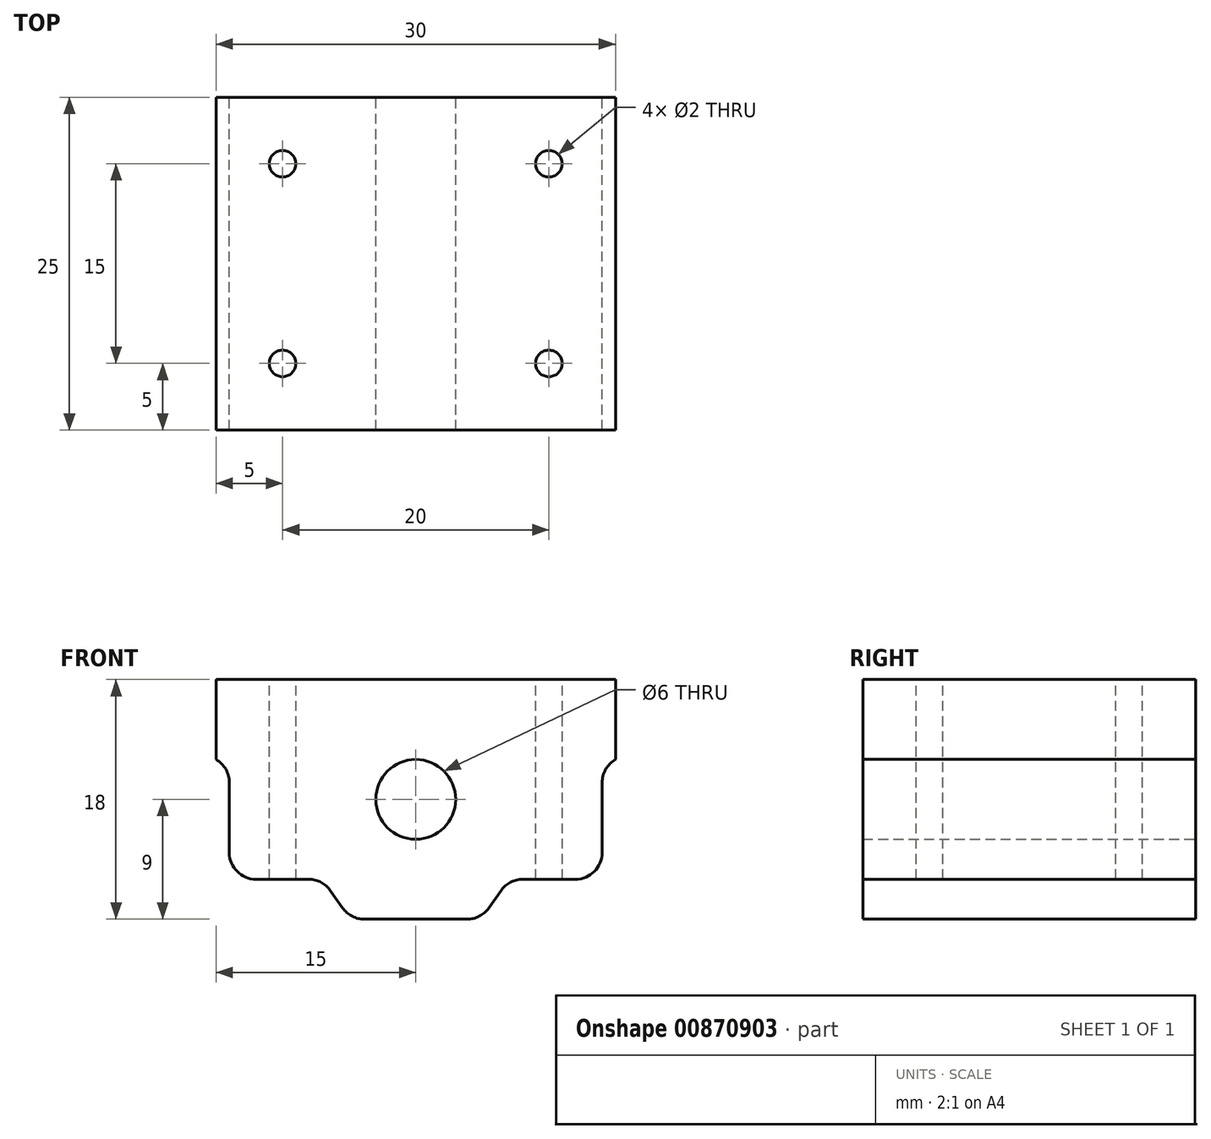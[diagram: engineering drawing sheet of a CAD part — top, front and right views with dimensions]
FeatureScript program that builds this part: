
annotation { "Feature Type Name" : "Feature", "Feature Type Description" : "" }
export const myFeature = defineFeature(function(context is Context, id is Id, definition is map)
    precondition{}
    {
        {
            var Q0;
            Q0=qCreatedBy(makeId("Front.planeOp"),FACE);
            var sketch = newSketch(context, id + "F0", { "sketchPlane" : qUnion([Q0])});
            skLineSegment(sketch, "E0", {"start": v(-15, 9) * mm, "end": v(15, 9) * mm});
            skPoint(sketch, "E1", {"position": v(0, 9) * mm});
            skCircle(sketch, "E2", {"center": v(0, 0) * mm, "radius": 3 * mm});
            skLineSegment(sketch, "E3", {"start": v(-15, 9) * mm, "end": v(-15, 3) * mm});
            skLineSegment(sketch, "E4", {"start": v(15, 9) * mm, "end": v(15, 3) * mm});
            skLineSegment(sketch, "E5", {"start": v(-15, 3) * mm, "end": v(-14, 3) * mm});
            skLineSegment(sketch, "E6", {"start": v(15, 3) * mm, "end": v(14, 3) * mm});
            skLineSegment(sketch, "E7", {"start": v(-14, 3) * mm, "end": v(-14, -6) * mm});
            skLineSegment(sketch, "E8", {"start": v(14, 3) * mm, "end": v(14, -6) * mm});
            skLineSegment(sketch, "E9", {"start": v(-4.9, -9) * mm, "end": v(4.9, -9) * mm});
            skPoint(sketch, "E10", {"position": v(0, -9) * mm});
            skLineSegment(sketch, "E11", {"start": v(14, -6) * mm, "end": v(7, -6) * mm});
            skLineSegment(sketch, "E12", {"start": v(-14, -6) * mm, "end": v(-7, -6) * mm});
            skLineSegment(sketch, "E13", {"start": v(4.9, -9) * mm, "end": v(7, -6) * mm});
            skLineSegment(sketch, "E14", {"start": v(-7, -6) * mm, "end": v(-4.9, -9) * mm});
            skSolve(sketch);
        }
        {
            var Q0;
            Q0=makeQuery(id+"F0.imprint","IMPRINT",FACE,{"disambiguationData":[TD([[makeQuery(id+"F0.imprint","IMPRINT",EDGE,{"derivedFrom":sQuery(id+"F0.wireOp",EDGE,"E0")}),-1.0]])]});
            extrude(context, id + "F1", {"entities" : qUnion([Q0]), "depth" : 25 * mm, "offsetDistance" : 25 * mm});
        }
        {
            var Q0;
            Q0=makeQuery(id+"F1.opExtrude","SWEPT_FACE",FACE,{"disambiguationData":[OSD([sQuery(id+"F0.wireOp",EDGE,"E0")])]});
            var sketch = newSketch(context, id + "F2", { "sketchPlane" : qUnion([Q0])});
            skPoint(sketch, "E15", {"position": v(0, -20) * mm});
            skPoint(sketch, "E15.positionSnap0", {"position": v(0, -25) * mm});
            skLineSegment(sketch, "E16", {"start": v(10, -20) * mm, "end": v(-10, -20) * mm});
            skLineSegment(sketch, "E17", {"start": v(10, -20) * mm, "end": v(10, -5) * mm});
            skLineSegment(sketch, "E18", {"start": v(10, -5) * mm, "end": v(-10, -5) * mm});
            skLineSegment(sketch, "E19", {"start": v(-10, -5) * mm, "end": v(-10, -20) * mm});
            skCircle(sketch, "E20", {"center": v(10, -20) * mm, "radius": 1 * mm});
            skCircle(sketch, "E21", {"center": v(-10, -20) * mm, "radius": 1 * mm});
            skCircle(sketch, "E22", {"center": v(-10, -5) * mm, "radius": 1 * mm});
            skCircle(sketch, "E23", {"center": v(10, -5) * mm, "radius": 1 * mm});
            skSolve(sketch);
        }
        {
            var Q0;
            {var subQ0=sQuery(id+"F2.wireOp",EDGE,"E18");var subQ1=sQuery(id+"F2.wireOp",EDGE,"E17");var subQ2=makeQuery(id+"F2.imprint","INTERSECT",VERTEX,{"derivedFrom":[subQ1,subQ0]});Q0=makeQuery(id+"F2.imprint","IMPRINT",FACE,{"disambiguationData":[TD([[makeQuery(id+"F2.imprint","IMPRINT",EDGE,{"disambiguationData":[TD([[subQ2,1.0]])],"derivedFrom":subQ1}),-1.0]])]});}
            var Q1;
            {var subQ0=sQuery(id+"F2.wireOp",EDGE,"E18");var subQ1=sQuery(id+"F2.wireOp",EDGE,"E17");var subQ2=makeQuery(id+"F2.imprint","INTERSECT",VERTEX,{"derivedFrom":[subQ1,subQ0]});Q1=makeQuery(id+"F2.imprint","IMPRINT",FACE,{"disambiguationData":[TD([[makeQuery(id+"F2.imprint","IMPRINT",EDGE,{"disambiguationData":[TD([[subQ2,1.0]])],"derivedFrom":subQ1}),1.0]])]});}
            var Q2;
            {var subQ0=sQuery(id+"F2.wireOp",EDGE,"E17");var subQ1=sQuery(id+"F2.wireOp",EDGE,"E16");var subQ2=makeQuery(id+"F2.imprint","INTERSECT",VERTEX,{"derivedFrom":[subQ1,subQ0]});Q2=makeQuery(id+"F2.imprint","IMPRINT",FACE,{"disambiguationData":[TD([[makeQuery(id+"F2.imprint","IMPRINT",EDGE,{"disambiguationData":[TD([[subQ2,-1.0]])],"derivedFrom":subQ1}),1.0]])]});}
            var Q3;
            {var subQ0=sQuery(id+"F2.wireOp",EDGE,"E17");var subQ1=sQuery(id+"F2.wireOp",EDGE,"E16");var subQ2=makeQuery(id+"F2.imprint","INTERSECT",VERTEX,{"derivedFrom":[subQ1,subQ0]});Q3=makeQuery(id+"F2.imprint","IMPRINT",FACE,{"disambiguationData":[TD([[makeQuery(id+"F2.imprint","IMPRINT",EDGE,{"disambiguationData":[TD([[subQ2,-1.0]])],"derivedFrom":subQ1}),-1.0]])]});}
            var Q4;
            {var subQ0=sQuery(id+"F2.wireOp",EDGE,"E19");var subQ1=sQuery(id+"F2.wireOp",EDGE,"E16");var subQ2=makeQuery(id+"F2.imprint","INTERSECT",VERTEX,{"derivedFrom":[subQ1,subQ0]});Q4=makeQuery(id+"F2.imprint","IMPRINT",FACE,{"disambiguationData":[TD([[makeQuery(id+"F2.imprint","IMPRINT",EDGE,{"disambiguationData":[TD([[subQ2,1.0]])],"derivedFrom":subQ1}),1.0]])]});}
            var Q5;
            {var subQ0=sQuery(id+"F2.wireOp",EDGE,"E19");var subQ1=sQuery(id+"F2.wireOp",EDGE,"E16");var subQ2=makeQuery(id+"F2.imprint","INTERSECT",VERTEX,{"derivedFrom":[subQ1,subQ0]});Q5=makeQuery(id+"F2.imprint","IMPRINT",FACE,{"disambiguationData":[TD([[makeQuery(id+"F2.imprint","IMPRINT",EDGE,{"disambiguationData":[TD([[subQ2,1.0]])],"derivedFrom":subQ1}),-1.0]])]});}
            var Q6;
            {var subQ0=sQuery(id+"F2.wireOp",EDGE,"E19");var subQ1=sQuery(id+"F2.wireOp",EDGE,"E18");var subQ2=makeQuery(id+"F2.imprint","INTERSECT",VERTEX,{"derivedFrom":[subQ1,subQ0]});Q6=makeQuery(id+"F2.imprint","IMPRINT",FACE,{"disambiguationData":[TD([[makeQuery(id+"F2.imprint","IMPRINT",EDGE,{"disambiguationData":[TD([[subQ2,1.0]])],"derivedFrom":subQ1}),-1.0]])]});}
            var Q7;
            {var subQ0=sQuery(id+"F2.wireOp",EDGE,"E19");var subQ1=sQuery(id+"F2.wireOp",EDGE,"E18");var subQ2=makeQuery(id+"F2.imprint","INTERSECT",VERTEX,{"derivedFrom":[subQ1,subQ0]});Q7=makeQuery(id+"F2.imprint","IMPRINT",FACE,{"disambiguationData":[TD([[makeQuery(id+"F2.imprint","IMPRINT",EDGE,{"disambiguationData":[TD([[subQ2,1.0]])],"derivedFrom":subQ1}),1.0]])]});}
            extrude(context, id + "F3", {"entities" : qUnion([Q0, Q1, Q2, Q3, Q4, Q5, Q6, Q7]), "operationType" : NewBodyOperationType.REMOVE, "endBound" : BoundingType.THROUGH_ALL, "oppositeDirection" : true, "depth" : 25 * mm, "offsetDistance" : 25 * mm});
        }
        {
            var Q0;
            Q0=makeQuery(id+"F1.opExtrude","SWEPT_EDGE",EDGE,{"disambiguationData":[OSD([sQuery(id+"F0.wireOp",EDGE,"E11"),sQuery(id+"F0.wireOp",EDGE,"E13")])]});
            var Q1;
            Q1=makeQuery(id+"F1.opExtrude","SWEPT_EDGE",EDGE,{"disambiguationData":[OSD([sQuery(id+"F0.wireOp",EDGE,"E12"),sQuery(id+"F0.wireOp",EDGE,"E14")])]});
            var Q2;
            Q2=makeQuery(id+"F1.opExtrude","SWEPT_EDGE",EDGE,{"disambiguationData":[OSD([sQuery(id+"F0.wireOp",EDGE,"E7"),sQuery(id+"F0.wireOp",EDGE,"E12")])]});
            var Q3;
            Q3=makeQuery(id+"F1.opExtrude","SWEPT_EDGE",EDGE,{"disambiguationData":[OSD([sQuery(id+"F0.wireOp",EDGE,"E8"),sQuery(id+"F0.wireOp",EDGE,"E11")])]});
            var Q4;
            Q4=makeQuery(id+"F1.opExtrude","SWEPT_EDGE",EDGE,{"disambiguationData":[OSD([sQuery(id+"F0.wireOp",EDGE,"E9"),sQuery(id+"F0.wireOp",EDGE,"E13")])]});
            var Q5;
            Q5=makeQuery(id+"F1.opExtrude","SWEPT_EDGE",EDGE,{"disambiguationData":[OSD([sQuery(id+"F0.wireOp",EDGE,"E9"),sQuery(id+"F0.wireOp",EDGE,"E14")])]});
            var Q6;
            Q6=makeQuery(id+"F1.opExtrude","SWEPT_EDGE",EDGE,{"disambiguationData":[OSD([sQuery(id+"F0.wireOp",EDGE,"E6"),sQuery(id+"F0.wireOp",EDGE,"E8")])]});
            var Q7;
            Q7=makeQuery(id+"F1.opExtrude","SWEPT_EDGE",EDGE,{"disambiguationData":[OSD([sQuery(id+"F0.wireOp",EDGE,"E5"),sQuery(id+"F0.wireOp",EDGE,"E7")])]});
            fillet(context, id + "F4", {"entities" : qUnion([Q0, Q1, Q2, Q3, Q4, Q5, Q6, Q7]), "radius" : 2 * mm, "tangentPropagation" : true, "allowEdgeOverflow" : false});
        }
    });
